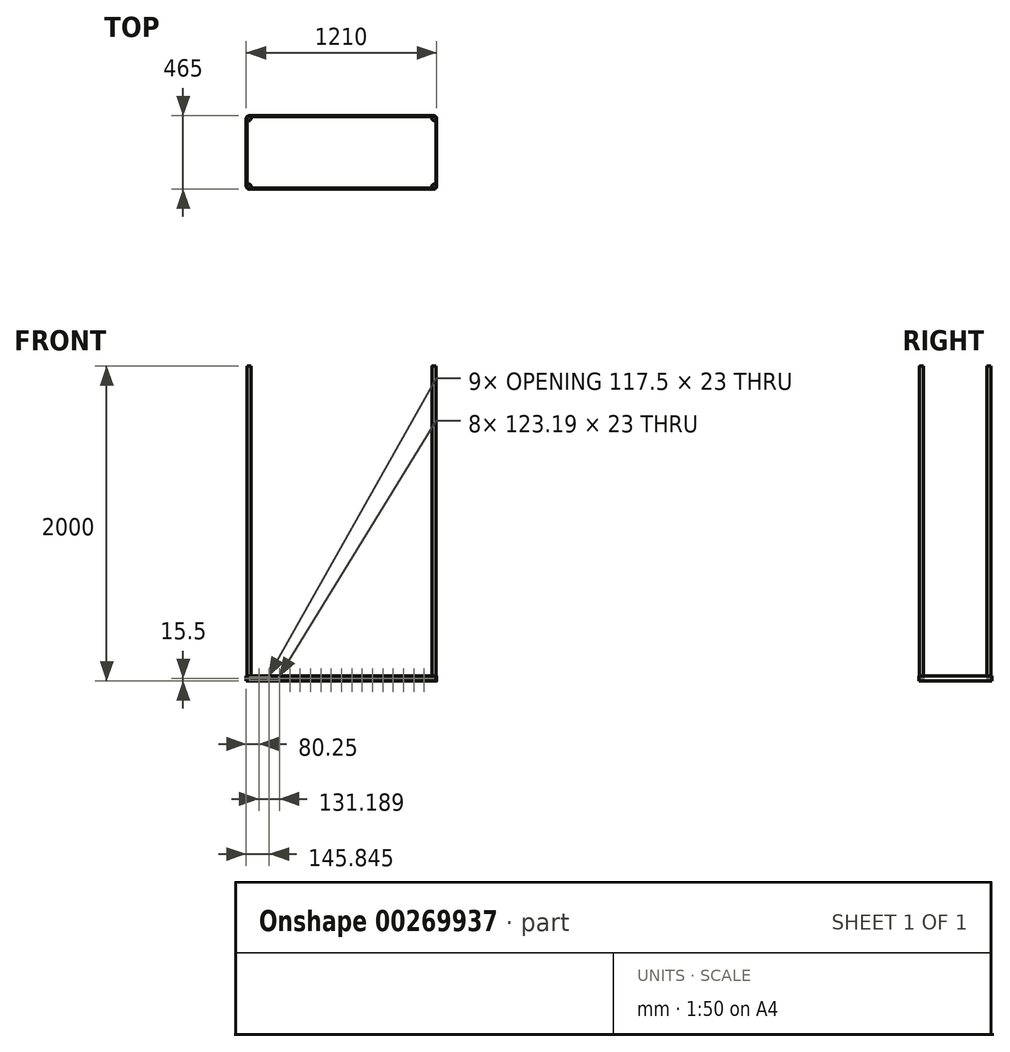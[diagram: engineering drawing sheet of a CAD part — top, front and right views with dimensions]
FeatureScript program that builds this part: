
annotation { "Feature Type Name" : "Feature", "Feature Type Description" : "" }
export const myFeature = defineFeature(function(context is Context, id is Id, definition is map)
    precondition{}
    {
        {
            var Q0;
            Q0=qCreatedBy(makeId("Top.planeOp"),FACE);
            var sketch = newSketch(context, id + "F0", { "sketchPlane" : qUnion([Q0])});
            skLineSegment(sketch, "E0.bottom", {"start": v(12.5, 0) * mm, "end": v(1187.5, 0) * mm});
            skLineSegment(sketch, "E0.top", {"start": v(12.5, 455) * mm, "end": v(1187.5, 455) * mm});
            skLineSegment(sketch, "E0.left", {"start": v(0, 12.5) * mm, "end": v(0, 442.5) * mm});
            skLineSegment(sketch, "E0.right", {"start": v(1200, 12.5) * mm, "end": v(1200, 442.5) * mm});
            skPoint(sketch, "E1.visualSharp", {"position": v(0, 455) * mm});
            skArc(sketch, "E1.filletArc", {"start": v(12.5, 455) * mm, "mid": v(3.66, 451.34) * mm, "end": v(0, 442.5) * mm});
            skPoint(sketch, "E2.visualSharp", {"position": v(0, 0) * mm});
            skArc(sketch, "E2.filletArc", {"start": v(0, 12.5) * mm, "mid": v(3.66, 3.66) * mm, "end": v(12.5, 0) * mm});
            skPoint(sketch, "E3.visualSharp", {"position": v(1200, 0) * mm});
            skArc(sketch, "E3.filletArc", {"start": v(1187.5, 0) * mm, "mid": v(1196.34, 3.66) * mm, "end": v(1200, 12.5) * mm});
            skPoint(sketch, "E4.visualSharp", {"position": v(1200, 455) * mm});
            skArc(sketch, "E4.filletArc", {"start": v(1200, 442.5) * mm, "mid": v(1196.34, 451.34) * mm, "end": v(1187.5, 455) * mm});
            skLineSegment(sketch, "E5.0", {"start": v(-5, 12.5) * mm, "end": v(-5, 442.5) * mm});
            skLineSegment(sketch, "E6.0", {"start": v(12.5, 460) * mm, "end": v(1187.5, 460) * mm});
            skLineSegment(sketch, "E7.0", {"start": v(1205, 12.5) * mm, "end": v(1205, 442.5) * mm});
            skLineSegment(sketch, "E8.0", {"start": v(12.5, -5) * mm, "end": v(1187.5, -5) * mm});
            skArc(sketch, "E9.0", {"start": v(-5, 12.5) * mm, "mid": v(0.13, 0.13) * mm, "end": v(12.5, -5) * mm});
            skArc(sketch, "E10.0", {"start": v(1187.5, -5) * mm, "mid": v(1199.87, 0.13) * mm, "end": v(1205, 12.5) * mm});
            skArc(sketch, "E11.0", {"start": v(1205, 442.5) * mm, "mid": v(1199.87, 454.87) * mm, "end": v(1187.5, 460) * mm});
            skArc(sketch, "E12.0", {"start": v(12.5, 460) * mm, "mid": v(0.13, 454.87) * mm, "end": v(-5, 442.5) * mm});
            skSolve(sketch);
        }
        {
            var Q0;
            Q0 = qSketchRegion(id + "F0", true);
            extrude(context, id + "F1", {"entities" : qUnion([Q0]), "depth" : 31 * mm});
        }
        {
            var Q0;
            Q0=qCreatedBy(makeId("Top.planeOp"),FACE);
            var sketch = newSketch(context, id + "F2", { "sketchPlane" : qUnion([Q0])});
            skLineSegment(sketch, "E13.0", {"start": v(5, -6.5) * mm, "end": v(1195, -6.5) * mm});
            skLineSegment(sketch, "E14.0", {"start": v(5, -3.5) * mm, "end": v(1195, -3.5) * mm});
            skPoint(sketch, "E15.orphan", {"position": v(15, -5) * mm});
            skPoint(sketch, "E16.orphan", {"position": v(82.5, 0) * mm});
            skPoint(sketch, "E17.end.orphan", {"position": v(135, -5) * mm});
            skCircle(sketch, "E18", {"center": v(12.72, 12.61) * mm, "radius": 12.75 * mm});
            skLineSegment(sketch, "E19.0", {"start": v(12.5, 455) * mm, "end": v(1187.5, 455) * mm, "construction": true});
            skLineSegment(sketch, "E20.0", {"start": v(0, 12.5) * mm, "end": v(0, 442.5) * mm, "construction": true});
            skLineSegment(sketch, "E21.0", {"start": v(12.5, 0) * mm, "end": v(1187.5, 0) * mm, "construction": true});
            skLineSegment(sketch, "E22.0", {"start": v(1200, 12.5) * mm, "end": v(1200, 442.5) * mm, "construction": true});
            skLineSegment(sketch, "E23", {"start": v(600, 455) * mm, "end": v(600, 0) * mm, "construction": true});
            skLineSegment(sketch, "E24", {"start": v(0, 227.5) * mm, "end": v(1200, 227.5) * mm, "construction": true});
            skCircle(sketch, "E25.MirrorC", {"center": v(12.72, 442.39) * mm, "radius": 12.75 * mm});
            skCircle(sketch, "E26.MirrorC", {"center": v(1187.28, 442.39) * mm, "radius": 12.75 * mm});
            skCircle(sketch, "E27.MirrorC", {"center": v(1187.28, 12.61) * mm, "radius": 12.75 * mm});
            skSolve(sketch);
        }
        {
            var Q0;
            Q0 = qSketchRegion(id + "F2", true);
            extrude(context, id + "F3", {"entities" : qUnion([Q0]), "operationType" : NewBodyOperationType.ADD, "depth" : 2000 * mm});
        }
        {
            var Q0;
            Q0=qCreatedBy(makeId("Front.planeOp"),FACE);
            var sketch = newSketch(context, id + "F4", { "sketchPlane" : qUnion([Q0])});
            skLineSegment(sketch, "E28.0", {"start": v(12.5, 29) * mm, "end": v(1187.5, 29) * mm});
            skLineSegment(sketch, "E29.0", {"start": v(12.5, 2) * mm, "end": v(1187.5, 2) * mm});
            skLineSegment(sketch, "E30", {"start": v(25.47, 2000) * mm, "end": v(25.47, 0) * mm, "construction": true});
            skLineSegment(sketch, "E31.0", {"start": v(12.5, 27) * mm, "end": v(1187.5, 27) * mm});
            skLineSegment(sketch, "E32.0", {"start": v(12.5, 4) * mm, "end": v(1187.5, 4) * mm});
            skLineSegment(sketch, "E33", {"start": v(12.5, 27) * mm, "end": v(71.25, 4) * mm});
            skLineSegment(sketch, "E34", {"start": v(16.5, 27) * mm, "end": v(75.25, 4) * mm});
            skLineSegment(sketch, "E35", {"start": v(75.25, 4) * mm, "end": v(134, 27) * mm});
            skLineSegment(sketch, "E36", {"start": v(79.25, 4) * mm, "end": v(138, 27) * mm});
            skLineSegment(sketch, "E37.1.0.0", {"start": v(143.69, 27) * mm, "end": v(202.44, 4) * mm});
            skLineSegment(sketch, "E37.1.0.1", {"start": v(147.69, 27) * mm, "end": v(206.44, 4) * mm});
            skLineSegment(sketch, "E37.1.0.2", {"start": v(206.44, 4) * mm, "end": v(265.19, 27) * mm});
            skLineSegment(sketch, "E37.1.0.3", {"start": v(210.44, 4) * mm, "end": v(269.19, 27) * mm});
            skLineSegment(sketch, "E37.2.0.0", {"start": v(274.88, 27) * mm, "end": v(333.63, 4) * mm});
            skLineSegment(sketch, "E37.2.0.1", {"start": v(278.88, 27) * mm, "end": v(337.63, 4) * mm});
            skLineSegment(sketch, "E37.2.0.2", {"start": v(337.63, 4) * mm, "end": v(396.38, 27) * mm});
            skLineSegment(sketch, "E37.2.0.3", {"start": v(341.63, 4) * mm, "end": v(400.38, 27) * mm});
            skLineSegment(sketch, "E37.3.0.0", {"start": v(406.07, 27) * mm, "end": v(464.82, 4) * mm});
            skLineSegment(sketch, "E37.3.0.1", {"start": v(410.07, 27) * mm, "end": v(468.82, 4) * mm});
            skLineSegment(sketch, "E37.3.0.2", {"start": v(468.82, 4) * mm, "end": v(527.57, 27) * mm});
            skLineSegment(sketch, "E37.3.0.3", {"start": v(472.82, 4) * mm, "end": v(531.57, 27) * mm});
            skLineSegment(sketch, "E37.4.0.0", {"start": v(537.26, 27) * mm, "end": v(596, 4) * mm});
            skLineSegment(sketch, "E37.4.0.1", {"start": v(541.26, 27) * mm, "end": v(600, 4) * mm});
            skLineSegment(sketch, "E37.4.0.2", {"start": v(600, 4) * mm, "end": v(658.76, 27) * mm});
            skLineSegment(sketch, "E37.4.0.3", {"start": v(604, 4) * mm, "end": v(662.76, 27) * mm});
            skLineSegment(sketch, "E37.5.0.0", {"start": v(668.44, 27) * mm, "end": v(727.2, 4) * mm});
            skLineSegment(sketch, "E37.5.0.1", {"start": v(672.44, 27) * mm, "end": v(731.2, 4) * mm});
            skLineSegment(sketch, "E37.5.0.2", {"start": v(731.2, 4) * mm, "end": v(789.94, 27) * mm});
            skLineSegment(sketch, "E37.5.0.3", {"start": v(735.2, 4) * mm, "end": v(793.94, 27) * mm});
            skLineSegment(sketch, "E37.6.0.0", {"start": v(799.63, 27) * mm, "end": v(858.38, 4) * mm});
            skLineSegment(sketch, "E37.6.0.1", {"start": v(803.63, 27) * mm, "end": v(862.38, 4) * mm});
            skLineSegment(sketch, "E37.6.0.2", {"start": v(862.38, 4) * mm, "end": v(921.13, 27) * mm});
            skLineSegment(sketch, "E37.6.0.3", {"start": v(866.38, 4) * mm, "end": v(925.13, 27) * mm});
            skLineSegment(sketch, "E37.7.0.0", {"start": v(930.82, 27) * mm, "end": v(989.57, 4) * mm});
            skLineSegment(sketch, "E37.7.0.1", {"start": v(934.82, 27) * mm, "end": v(993.57, 4) * mm});
            skLineSegment(sketch, "E37.7.0.2", {"start": v(993.57, 4) * mm, "end": v(1052.32, 27) * mm});
            skLineSegment(sketch, "E37.7.0.3", {"start": v(997.57, 4) * mm, "end": v(1056.32, 27) * mm});
            skLineSegment(sketch, "E37.8.0.0", {"start": v(1062.01, 27) * mm, "end": v(1120.76, 4) * mm});
            skLineSegment(sketch, "E37.8.0.1", {"start": v(1066.01, 27) * mm, "end": v(1124.76, 4) * mm});
            skLineSegment(sketch, "E37.8.0.2", {"start": v(1124.76, 4) * mm, "end": v(1183.51, 27) * mm});
            skLineSegment(sketch, "E37.8.0.3", {"start": v(1128.76, 4) * mm, "end": v(1187.51, 27) * mm});
            skLineSegment(sketch, "E37.direction1", {"start": v(12.5, 27) * mm, "end": v(143.69, 27) * mm, "construction": true});
            skLineSegment(sketch, "E38", {"start": v(12.5, 27) * mm, "end": v(12.5, 4) * mm});
            skLineSegment(sketch, "E39.0", {"start": v(1187.5, 31) * mm, "end": v(1187.5, 0) * mm});
            skSolve(sketch);
        }
        {
            var Q0;
            {var subQ0=sQuery(id+"F4.wireOp",EDGE,"E39.0");var subQ1=sQuery(id+"F4.wireOp",EDGE,"E32.0");var subQ2=makeQuery(id+"F4.imprint","INTERSECT",VERTEX,{"derivedFrom":[subQ1,subQ0]});Q0=makeQuery(id+"F4.imprint","IMPRINT",FACE,{"disambiguationData":[TD([[makeQuery(id+"F4.imprint","IMPRINT",EDGE,{"disambiguationData":[TD([[subQ2,1.0]])],"derivedFrom":subQ1}),1.0]])]});}
            var Q1;
            {var subQ0=sQuery(id+"F4.wireOp",EDGE,"E37.8.0.1");Q1=makeQuery(id+"F4.imprint","IMPRINT",FACE,{"disambiguationData":[TD([[makeQuery(id+"F4.imprint","IMPRINT",EDGE,{"derivedFrom":subQ0}),1.0]])]});}
            var Q2;
            {var subQ0=sQuery(id+"F4.wireOp",EDGE,"E37.7.0.3");Q2=makeQuery(id+"F4.imprint","IMPRINT",FACE,{"disambiguationData":[TD([[makeQuery(id+"F4.imprint","IMPRINT",EDGE,{"derivedFrom":subQ0}),-1.0]])]});}
            var Q3;
            {var subQ0=sQuery(id+"F4.wireOp",EDGE,"E37.7.0.1");Q3=makeQuery(id+"F4.imprint","IMPRINT",FACE,{"disambiguationData":[TD([[makeQuery(id+"F4.imprint","IMPRINT",EDGE,{"derivedFrom":subQ0}),1.0]])]});}
            var Q4;
            {var subQ0=sQuery(id+"F4.wireOp",EDGE,"E37.6.0.3");Q4=makeQuery(id+"F4.imprint","IMPRINT",FACE,{"disambiguationData":[TD([[makeQuery(id+"F4.imprint","IMPRINT",EDGE,{"derivedFrom":subQ0}),-1.0]])]});}
            var Q5;
            {var subQ0=sQuery(id+"F4.wireOp",EDGE,"E37.6.0.1");Q5=makeQuery(id+"F4.imprint","IMPRINT",FACE,{"disambiguationData":[TD([[makeQuery(id+"F4.imprint","IMPRINT",EDGE,{"derivedFrom":subQ0}),1.0]])]});}
            var Q6;
            {var subQ0=sQuery(id+"F4.wireOp",EDGE,"E37.5.0.3");Q6=makeQuery(id+"F4.imprint","IMPRINT",FACE,{"disambiguationData":[TD([[makeQuery(id+"F4.imprint","IMPRINT",EDGE,{"derivedFrom":subQ0}),-1.0]])]});}
            var Q7;
            {var subQ0=sQuery(id+"F4.wireOp",EDGE,"E37.5.0.1");Q7=makeQuery(id+"F4.imprint","IMPRINT",FACE,{"disambiguationData":[TD([[makeQuery(id+"F4.imprint","IMPRINT",EDGE,{"derivedFrom":subQ0}),1.0]])]});}
            var Q8;
            {var subQ0=sQuery(id+"F4.wireOp",EDGE,"E37.4.0.3");Q8=makeQuery(id+"F4.imprint","IMPRINT",FACE,{"disambiguationData":[TD([[makeQuery(id+"F4.imprint","IMPRINT",EDGE,{"derivedFrom":subQ0}),-1.0]])]});}
            var Q9;
            {var subQ0=sQuery(id+"F4.wireOp",EDGE,"E37.4.0.1");Q9=makeQuery(id+"F4.imprint","IMPRINT",FACE,{"disambiguationData":[TD([[makeQuery(id+"F4.imprint","IMPRINT",EDGE,{"derivedFrom":subQ0}),1.0]])]});}
            var Q10;
            {var subQ0=sQuery(id+"F4.wireOp",EDGE,"E37.3.0.3");Q10=makeQuery(id+"F4.imprint","IMPRINT",FACE,{"disambiguationData":[TD([[makeQuery(id+"F4.imprint","IMPRINT",EDGE,{"derivedFrom":subQ0}),-1.0]])]});}
            var Q11;
            {var subQ0=sQuery(id+"F4.wireOp",EDGE,"E37.3.0.1");Q11=makeQuery(id+"F4.imprint","IMPRINT",FACE,{"disambiguationData":[TD([[makeQuery(id+"F4.imprint","IMPRINT",EDGE,{"derivedFrom":subQ0}),1.0]])]});}
            var Q12;
            {var subQ0=sQuery(id+"F4.wireOp",EDGE,"E37.2.0.3");Q12=makeQuery(id+"F4.imprint","IMPRINT",FACE,{"disambiguationData":[TD([[makeQuery(id+"F4.imprint","IMPRINT",EDGE,{"derivedFrom":subQ0}),-1.0]])]});}
            var Q13;
            {var subQ0=sQuery(id+"F4.wireOp",EDGE,"E37.2.0.1");Q13=makeQuery(id+"F4.imprint","IMPRINT",FACE,{"disambiguationData":[TD([[makeQuery(id+"F4.imprint","IMPRINT",EDGE,{"derivedFrom":subQ0}),1.0]])]});}
            var Q14;
            {var subQ0=sQuery(id+"F4.wireOp",EDGE,"E37.1.0.3");Q14=makeQuery(id+"F4.imprint","IMPRINT",FACE,{"disambiguationData":[TD([[makeQuery(id+"F4.imprint","IMPRINT",EDGE,{"derivedFrom":subQ0}),-1.0]])]});}
            var Q15;
            {var subQ0=sQuery(id+"F4.wireOp",EDGE,"E37.1.0.1");Q15=makeQuery(id+"F4.imprint","IMPRINT",FACE,{"disambiguationData":[TD([[makeQuery(id+"F4.imprint","IMPRINT",EDGE,{"derivedFrom":subQ0}),1.0]])]});}
            var Q16;
            {var subQ0=sQuery(id+"F4.wireOp",EDGE,"E36");Q16=makeQuery(id+"F4.imprint","IMPRINT",FACE,{"disambiguationData":[TD([[makeQuery(id+"F4.imprint","IMPRINT",EDGE,{"derivedFrom":subQ0}),-1.0]])]});}
            var Q17;
            {var subQ0=sQuery(id+"F4.wireOp",EDGE,"E34");Q17=makeQuery(id+"F4.imprint","IMPRINT",FACE,{"disambiguationData":[TD([[makeQuery(id+"F4.imprint","IMPRINT",EDGE,{"derivedFrom":subQ0}),1.0]])]});}
            var Q18;
            {var subQ2=sQuery(id+"F4.wireOp",EDGE,"E33");Q18=makeQuery(id+"F4.imprint","IMPRINT",FACE,{"disambiguationData":[TD([[makeQuery(id+"F4.imprint","IMPRINT",EDGE,{"derivedFrom":subQ2}),-1.0]])]});}
            extrude(context, id + "F5", {"entities" : qUnion([Q0, Q1, Q2, Q3, Q4, Q5, Q6, Q7, Q8, Q9, Q10, Q11, Q12, Q13, Q14, Q15, Q16, Q17, Q18]), "operationType" : NewBodyOperationType.REMOVE, "depth" : 25 * mm});
        }
    });
